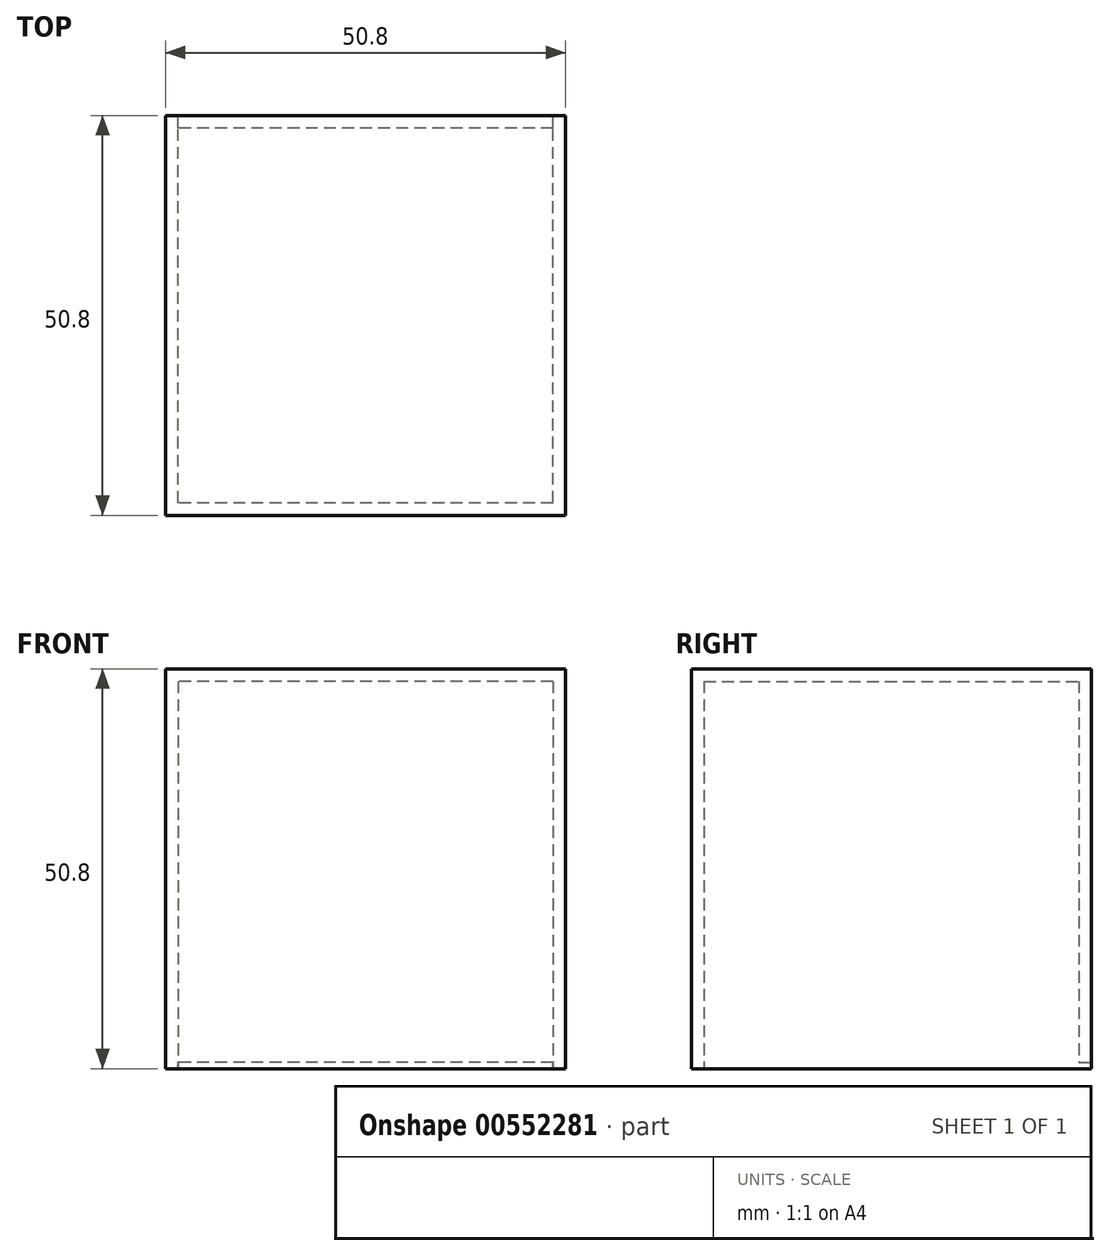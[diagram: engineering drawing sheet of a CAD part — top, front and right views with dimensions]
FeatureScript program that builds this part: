
annotation { "Feature Type Name" : "Feature", "Feature Type Description" : "" }
export const myFeature = defineFeature(function(context is Context, id is Id, definition is map)
    precondition{}
    {
        {
            var Q0;
            Q0=qCreatedBy(makeId("Right.planeOp"),FACE);
            var sketch = newSketch(context, id + "F0", { "sketchPlane" : qUnion([Q0])});
            skLineSegment(sketch, "E0.bottom", {"start": v(-29.41, 41.14) * mm, "end": v(21.39, 41.14) * mm});
            skLineSegment(sketch, "E0.top", {"start": v(-29.41, -9.66) * mm, "end": v(21.39, -9.66) * mm});
            skLineSegment(sketch, "E0.left", {"start": v(-29.41, 41.14) * mm, "end": v(-29.41, -9.66) * mm});
            skLineSegment(sketch, "E0.right", {"start": v(21.39, 41.14) * mm, "end": v(21.39, -9.66) * mm});
            skSolve(sketch);
        }
        {
            var Q0;
            Q0 = qSketchRegion(id + "F0", true);
            extrude(context, id + "F1", {"entities" : qUnion([Q0]), "depth" : 50.8 * mm, "offsetDistance" : 25.4 * mm});
        }
        {
            var Q0;
            Q0=makeQuery(id+"F1.opExtrude","SWEPT_FACE",FACE,{"disambiguationData":[OSD([sQuery(id+"F0.wireOp",EDGE,"E0.top")])]});
            shell(context, id + "F2", {"entities" : qUnion([Q0]), "thickness" : 1.59 * mm});
        }
        {
            var Q0;
            Q0=makeQuery(id+"F1.opExtrude","SWEPT_FACE",FACE,{"disambiguationData":[OSD([sQuery(id+"F0.wireOp",EDGE,"E0.right")])]});
            var sketch = newSketch(context, id + "F3", { "sketchPlane" : qUnion([Q0])});
            skLineSegment(sketch, "E1.bottom", {"start": v(-49.21, -9.66) * mm, "end": v(-1.59, -9.66) * mm});
            skLineSegment(sketch, "E1.top", {"start": v(-49.21, -8.86) * mm, "end": v(-1.59, -8.86) * mm});
            skLineSegment(sketch, "E1.left", {"start": v(-49.21, -9.66) * mm, "end": v(-49.21, -8.86) * mm});
            skLineSegment(sketch, "E1.right", {"start": v(-1.59, -9.66) * mm, "end": v(-1.59, -8.86) * mm});
            skSolve(sketch);
        }
        {
            var Q0;
            Q0 = qSketchRegion(id + "F3", true);
            extrude(context, id + "F4", {"entities" : qUnion([Q0]), "operationType" : NewBodyOperationType.REMOVE, "oppositeDirection" : true, "depth" : 5.08 * mm, "offsetDistance" : 25.4 * mm});
        }
        {
            var Q0;
            Q0=makeQuery(id+"F1.opExtrude","SWEPT_BODY",BODY,{"disambiguationData":[OSD([sQuery(id+"F0.wireOp",EDGE,"E0.bottom"),sQuery(id+"F0.wireOp",EDGE,"E0.top"),sQuery(id+"F0.wireOp",EDGE,"E0.left"),sQuery(id+"F0.wireOp",EDGE,"E0.right")])]});
            transform(context, id + "F5", {"entities" : qUnion([Q0]), "transformType" : TransformType.TRANSLATION_3D, "dx" : 0 * mm, "dy" : 0 * mm, "dz" : 0 * mm, "makeCopy" : true});
        }
        {
            var Q0;
            Q0=makeQuery(id+"F5.opPattern","COPY",BODY,{"derivedFrom":makeQuery(id+"F1.opExtrude","SWEPT_BODY",BODY,{"disambiguationData":[OSD([sQuery(id+"F0.wireOp",EDGE,"E0.bottom"),sQuery(id+"F0.wireOp",EDGE,"E0.top"),sQuery(id+"F0.wireOp",EDGE,"E0.left"),sQuery(id+"F0.wireOp",EDGE,"E0.right")])]}),"instanceName":"1"});
            deleteBodies(context, id + "F6", {"entities" : qUnion([Q0])});
        }
        {
            var Q0;
            Q0=makeQuery(id+"F1.opExtrude","SWEPT_FACE",FACE,{"disambiguationData":[OSD([sQuery(id+"F0.wireOp",EDGE,"E0.top")])]});
            var Q1;
            Q1=makeQuery(id+"F4.boolean.opBoolean","COPY",FACE,{"derivedFrom":makeQuery(id+"F4.opExtrude","SWEPT_FACE",FACE,{"disambiguationData":[OSD([sQuery(id+"F3.wireOp",EDGE,"E1.top")])]})});
            extrude(context, id + "F7", {"entities" : qUnion([Q0, Q1]), "operationType" : NewBodyOperationType.ADD, "depth" : 1 / 812.8 * mm, "offsetDistance" : 25.4 * mm});
        }
    });
